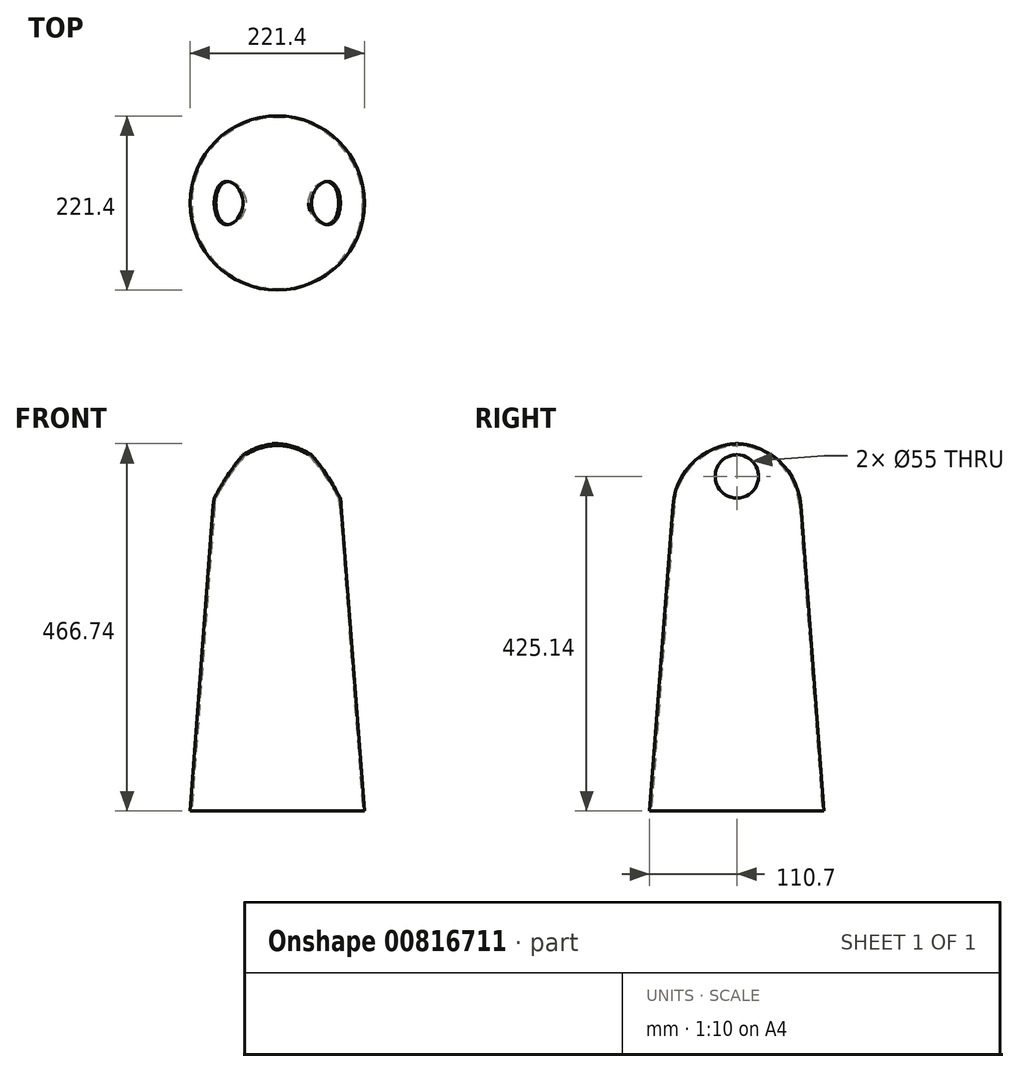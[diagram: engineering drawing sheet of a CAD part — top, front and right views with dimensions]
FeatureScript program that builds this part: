
annotation { "Feature Type Name" : "Feature", "Feature Type Description" : "" }
export const myFeature = defineFeature(function(context is Context, id is Id, definition is map)
    precondition{}
    {
        {
            var Q0;
            Q0=qCreatedBy(makeId("Front.planeOp"),FACE);
            var sketch = newSketch(context, id + "F0", { "sketchPlane" : qUnion([Q0])});
            skLineSegment(sketch, "E0", {"start": v(0, 0) * mm, "end": v(0, 388.14) * mm});
            skLineSegment(sketch, "E1", {"start": v(0, 0) * mm, "end": v(110.7, 0) * mm});
            skLineSegment(sketch, "E2", {"start": v(0, 388.14) * mm, "end": v(81.37, 388.14) * mm});
            skLineSegment(sketch, "E3", {"start": v(110.7, 0) * mm, "end": v(81.37, 388.14) * mm});
            skLineSegment(sketch, "E4", {"start": v(0, 466.67) * mm, "end": v(0, 388.14) * mm});
            skArc(sketch, "E5", {"start": v(81.37, 388.14) * mm, "mid": v(55.64, 442.9) * mm, "end": v(0, 466.67) * mm});
            skSolve(sketch);
        }
        {
            var Q0;
            Q0=makeQuery(id+"F0.imprint","IMPRINT",FACE,{"disambiguationData":[TD([[makeQuery(id+"F0.imprint","IMPRINT",EDGE,{"derivedFrom":sQuery(id+"F0.wireOp",EDGE,"E0")}),-1.0]])]});
            var Q1;
            Q1=makeQuery(id+"F0.imprint","IMPRINT",FACE,{"disambiguationData":[TD([[makeQuery(id+"F0.imprint","IMPRINT",EDGE,{"derivedFrom":sQuery(id+"F0.wireOp",EDGE,"E2")}),1.0]])]});
            var Q2;
            Q2=sQuery(id+"F0.wireOp",EDGE,"E0");
            revolve(context, id + "F1", {"surfaceOperationType" : NewSurfaceOperationType.NEW, "entities" : qUnion([Q0, Q1]), "axis" : qUnion([Q2]), "revolveType" : RevolveType.FULL});
        }
        {
            var Q0;
            Q0=makeQuery(id+"F1.opRevolve","SWEPT_FACE",FACE,{"disambiguationData":[OSD([sQuery(id+"F0.wireOp",EDGE,"E1")])]});
            shell(context, id + "F2", {"entities" : qUnion([Q0]), "thickness" : 2 * mm});
        }
        {
            var Q0;
            Q0=qCreatedBy(makeId("Right.planeOp"),FACE);
            cPlane(context, id + "F3", {"entities" : qUnion([Q0]), "cplaneType" : CPlaneType.OFFSET, "offset" : 111 * mm, "oppositeDirection" : true, "width" : 150 * mm, "height" : 150 * mm});
        }
        {
            var Q0;
            Q0=qCreatedBy(id+"F3.planeOp",FACE);
            var sketch = newSketch(context, id + "F4", { "sketchPlane" : qUnion([Q0])});
            skCircle(sketch, "E6", {"center": v(0, 425.14) * mm, "radius": 27.5 * mm});
            skSolve(sketch);
        }
        {
            var Q0;
            Q0=makeQuery(id+"F4.imprint","IMPRINT",FACE,{"disambiguationData":[TD([[makeQuery(id+"F4.imprint","IMPRINT",EDGE,{"derivedFrom":sQuery(id+"F4.wireOp",EDGE,"E6")}),1.0]])]});
            extrude(context, id + "F5", {"entities" : qUnion([Q0]), "operationType" : NewBodyOperationType.REMOVE, "depth" : 223 * mm, "offsetDistance" : 25 * mm});
        }
    });
